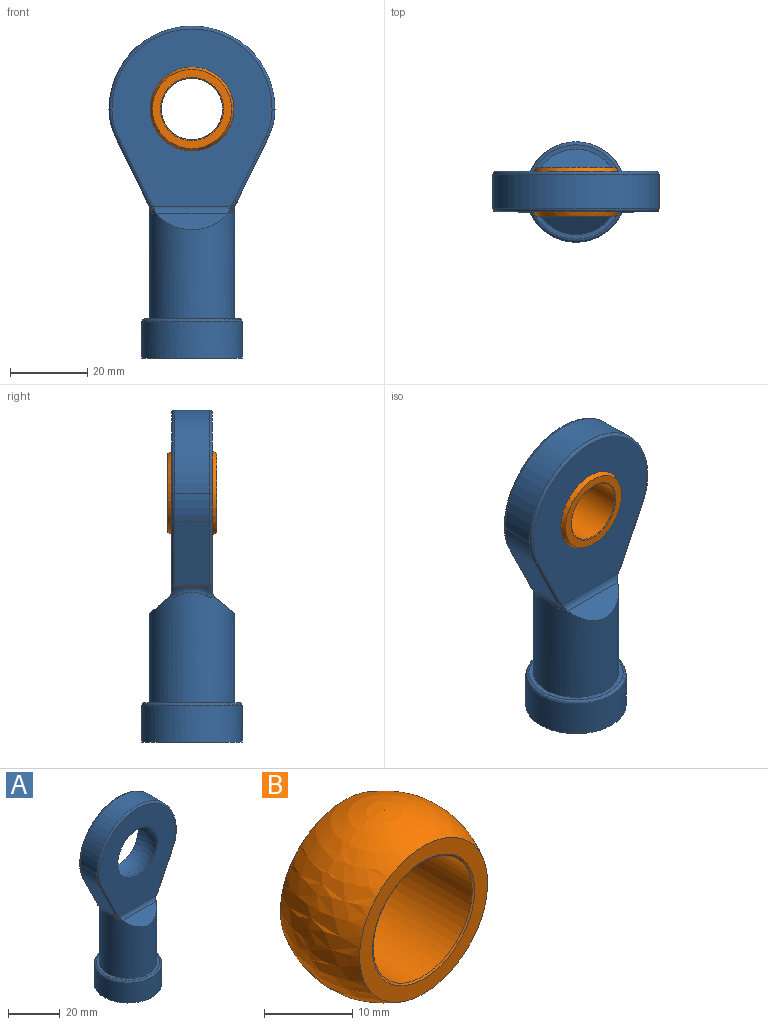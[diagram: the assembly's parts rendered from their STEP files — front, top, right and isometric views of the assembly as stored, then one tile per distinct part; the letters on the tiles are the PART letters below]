
ASSEMBLY  parts=2 mates=1
PART A: 50 faces, bbox 47.2x28.8x88.4 mm
  f0: cylinder r=11.05mm len=28.65mm, axis (0,0,-1), area 1792.5mm2, adj f1,f8,f9,f42,f43,f44,f45,f46
  f1: plane 24.46x24.46mm, normal (0,0,1), area 86.4mm2, adj f0,f2
  f2: torus R=12.23mm, axis (0,0,1), area 95.6mm2, adj f1,f3
  f3: cylinder r=12.99mm len=25.98mm, axis (0,0,-1), area 767.2mm2, adj f2,f4
  f4: plane 25.98x25.98mm, normal (0,0,-1), area 332.4mm2, adj f3,f5
  f5: cylinder r=7.94mm len=28.85mm, axis (0,0,-1), area 1438.8mm2, adj f4,f6
  f6: torus R=4.53mm, axis (0,0,-1), area 225.4mm2, adj f5,f7
  f7: plane 9.06x9.06mm, normal (0,0,-1), area 64.4mm2, adj f6
  f8: plane 18.35x4.89mm, normal (0,0.64,0.77), area 82.4mm2, adj f0,f49
  f9: bspline ~2.83x2.6mm, area 2.7mm2, adj f0,f10,f42,f49
  f10: cylinder r=0.76mm len=2.09mm, axis (-0.59,0,0.81), area 1.9mm2, adj f9,f11,f41
  f11: plane 8.98x1.25mm, normal (-0.81,0,-0.59), area 5.9mm2, adj f10,f12,f40,f42
  f12: cylinder r=0.76mm len=8.98mm, axis (0,-1,0), area 1.2mm2, adj f11,f13,f39,f41
  f13: sphere r=0.76mm, area 0.1mm2, adj f12,f14,f40
  f14: cylinder r=0.76mm len=17.03mm, axis (-0.44,0,0.9), area 22.2mm2, adj f13,f15,f37,f39
  f15: torus R=16.07mm, axis (0,-1,0), area 9mm2, adj f14,f16,f36,f37
  f16: cylinder r=16.83mm len=8.98mm, axis (0,1,0), area 68.4mm2, adj f15,f17,f35,f39
  f17: torus R=16.07mm, axis (0,-1,0), area 9mm2, adj f16,f18,f33,f34
  f18: plane 46.69x42.13mm, normal (0,1,0), area 1130.8mm2, adj f17,f19,f29,f30,f31,f32,f33,f34
  f19: cylinder r=0.76mm len=17.03mm, axis (0.44,0,0.9), area 22.2mm2, adj f18,f20,f28,f29
  f20: plane 16.69x8.98mm, normal (0.9,0,-0.44), area 166.6mm2, adj f19,f21,f26,f27
  f21: cylinder r=0.76mm len=17.81mm, axis (-0.44,0,-0.9), area 23.2mm2, adj f20,f22,f23,f37
  f22: torus R=16.07mm, axis (0,-1,0), area 9mm2, adj f21,f26,f36,f37
  f23: sphere r=0.76mm, area 0.1mm2, adj f21,f24,f27
  f24: cylinder r=0.76mm len=2.09mm, axis (-0.59,0,-0.81), area 1mm2, adj f23,f25,f46
  f25: plane 8.98x1.25mm, normal (0.81,0,-0.59), area 5.9mm2, adj f24,f27,f31,f47
  f26: cylinder r=16.83mm len=8.98mm, axis (0,1,0), area 68.4mm2, adj f20,f22,f29,f35
  f27: cylinder r=0.76mm len=8.98mm, axis (0,1,0), area 1.2mm2, adj f20,f23,f25,f28
  f28: sphere r=0.76mm, area 0.1mm2, adj f19,f27,f31
  f29: torus R=16.07mm, axis (0,-1,0), area 9mm2, adj f18,f19,f26,f33
  f30: bspline ~1.33x0.75mm, area 0.4mm2, adj f18,f31,f48,f49
  f31: cylinder r=0.76mm len=2.15mm, axis (-0.59,0,-0.81), area 2.3mm2, adj f18,f25,f28,f30,f48
  f32: sphere r=12.06mm, area 796.1mm2, adj f18,f37
  f33: torus R=20.74mm, axis (0,-1,0), area 79.8mm2, adj f17,f18,f29,f35
  f34: cylinder r=0.76mm len=17.81mm, axis (0.44,0,-0.9), area 23.2mm2, adj f17,f18,f39,f41
  f35: cylinder r=21.5mm len=43mm, axis (0,1,0), area 606.3mm2, adj f16,f26,f33,f36
  f36: torus R=20.74mm, axis (0,-1,0), area 79.8mm2, adj f15,f22,f35,f37
  f37: plane 46.69x42.13mm, normal (0,-1,0), area 1100.5mm2, adj f14,f15,f21,f22,f32,f36,f38,f40
  f38: bspline ~1.33x0.75mm, area 0.4mm2, adj f37,f40,f43,f45
  f39: plane 16.69x8.98mm, normal (-0.9,0,-0.44), area 166.6mm2, adj f12,f14,f16,f34
  f40: cylinder r=0.76mm len=2.15mm, axis (-0.59,0,0.81), area 2.3mm2, adj f11,f13,f37,f38,f43
  f41: sphere r=0.76mm, area 0.1mm2, adj f10,f12,f34
  f42: bspline ~8.98x2.41mm, area 13mm2, adj f0,f9,f11,f43
  f43: bspline ~2.33x1.86mm, area 2.1mm2, adj f0,f38,f40,f42
  f44: plane 18.35x4.89mm, normal (0,-0.64,0.77), area 82.4mm2, adj f0,f45
  f45: cylinder r=2.54mm len=20.31mm, axis (-1,0,0), area 42.5mm2, adj f0,f37,f38,f44,f46
  f46: bspline ~2.83x2.6mm, area 2.7mm2, adj f0,f24,f45,f47
  f47: bspline ~8.98x2.41mm, area 13mm2, adj f0,f25,f46,f48
  f48: bspline ~2.33x1.86mm, area 2.1mm2, adj f0,f30,f31,f47
  f49: cylinder r=2.54mm len=20.31mm, axis (-1,0,0), area 43.4mm2, adj f0,f8,f9,f18,f30
PART B: 5 faces, bbox 24.1x24.1x24.1 mm
  f0: sphere r=12.06mm, area 962.7mm2, adj f1,f2
  f1: plane 20.52x20.52mm, normal (0,-1,0), area 119.8mm2, adj f0,f4
  f2: plane 20.52x20.52mm, normal (0,1,0), area 132.7mm2, adj f0,f3
  f3: cylinder r=7.94mm len=15.88mm, axis (0,-1,0), area 626.1mm2, adj f2,f4
  f4: cone r=7.94mm half-angle=60deg, axis (0,-1,0), area 14.9mm2, adj f1,f3
PLACE A at identity fixed
PLACE B t=(0,-0.07,64.5)mm
MATE ball B.f3 <-> A.f33  axis (0,-1,0) through (0,0,64.5)mm
